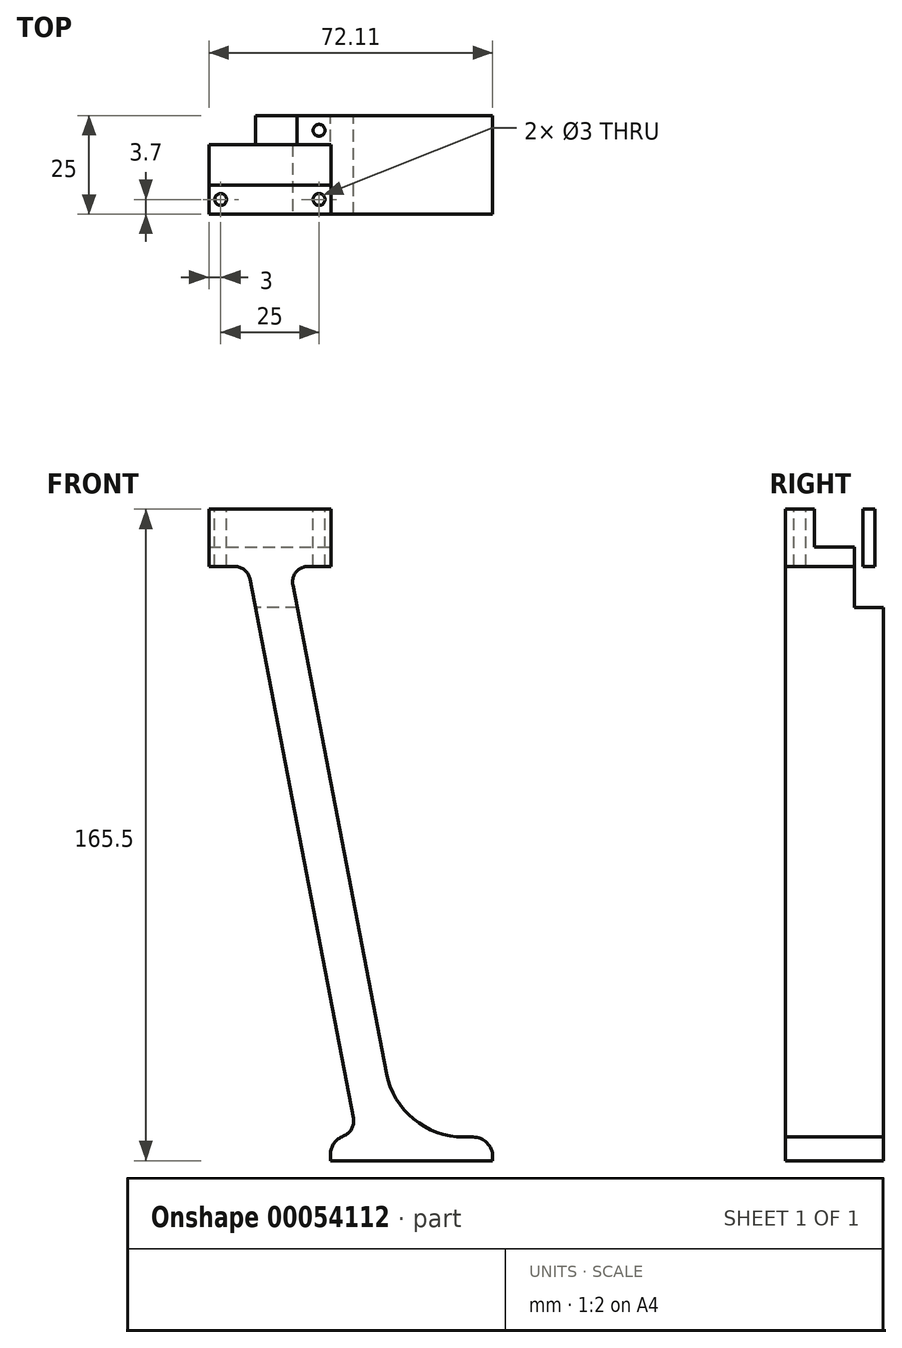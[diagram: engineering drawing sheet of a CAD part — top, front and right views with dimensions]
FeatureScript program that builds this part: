
annotation { "Feature Type Name" : "Feature", "Feature Type Description" : "" }
export const myFeature = defineFeature(function(context is Context, id is Id, definition is map)
    precondition{}
    {
        {
            var Q0;
            Q0=qCreatedBy(makeId("Front.planeOp"),FACE);
            var sketch = newSketch(context, id + "F0", { "sketchPlane" : qUnion([Q0])});
            skLineSegment(sketch, "E0.rect.bottom", {"start": v(12.5, -10) * mm, "end": v(1.92, -10) * mm});
            skLineSegment(sketch, "E0.rect.left", {"start": v(12.5, -10) * mm, "end": v(12.5, 4.5) * mm});
            skLineSegment(sketch, "E0.rect.right", {"start": v(-12.5, -10) * mm, "end": v(-12.5, 4.5) * mm});
            skPoint(sketch, "E0.rect.middle", {"position": v(0, 0) * mm});
            skLineSegment(sketch, "E1", {"start": v(-8.66, -10) * mm, "end": v(19.14, -155) * mm});
            skPoint(sketch, "E1.startSnap0", {"position": v(-12.5, 0) * mm});
            skLineSegment(sketch, "E2", {"start": v(1.92, -10) * mm, "end": v(29.71, -155) * mm});
            skPoint(sketch, "E3.orphan", {"position": v(-10.58, 0) * mm});
            skLineSegment(sketch, "E4.trimOffspring", {"start": v(-8.66, -10) * mm, "end": v(-12.5, -10) * mm});
            skLineSegment(sketch, "E5.bottom", {"start": v(12.4, -155) * mm, "end": v(19.14, -155) * mm});
            skLineSegment(sketch, "E5.top", {"start": v(12.4, -161) * mm, "end": v(53.6, -161) * mm});
            skLineSegment(sketch, "E5.left", {"start": v(12.4, -155) * mm, "end": v(12.4, -161) * mm});
            skLineSegment(sketch, "E5.right", {"start": v(53.6, -155) * mm, "end": v(53.6, -161) * mm});
            skLineSegment(sketch, "E6.trimOffspring", {"start": v(29.71, -155) * mm, "end": v(53.6, -155) * mm});
            skLineSegment(sketch, "E7", {"start": v(12.5, 4.5) * mm, "end": v(-12.5, 4.5) * mm});
            skPoint(sketch, "E8.orphan", {"position": v(12.5, 10) * mm});
            skPoint(sketch, "E9.orphan", {"position": v(-12.5, 10) * mm});
            skSolve(sketch);
        }
        {
            var Q0;
            Q0=makeQuery(id+"F0.imprint","IMPRINT",FACE,{"disambiguationData":[TD([[makeQuery(id+"F0.imprint","IMPRINT",EDGE,{"derivedFrom":sQuery(id+"F0.wireOp",EDGE,"E0.rect.bottom")}),-1.0]])]});
            var Q1;
            Q1 = qSketchRegion(id + "F2", true);
            extrude(context, id + "F1", {"entities" : qUnion([Q0, Q1]), "depth" : 25 * mm});
        }
        {
            var Q0;
            Q0=makeQuery(id+"F1.opExtrude","SWEPT_FACE",FACE,{"disambiguationData":[OSD([sQuery(id+"F0.wireOp",EDGE,"E0.rect.left")])]});
            var sketch = newSketch(context, id + "F2", { "sketchPlane" : qUnion([Q0])});
            skPoint(sketch, "E10.centerSnap0", {"position": v(-12.5, -10) * mm});
            skLineSegment(sketch, "E11.rect.bottom", {"start": v(-7.4, -5.1) * mm, "end": v(-17.6, -5.1) * mm});
            skLineSegment(sketch, "E11.rect.top", {"start": v(-7.4, 5.1) * mm, "end": v(-17.6, 5.1) * mm});
            skLineSegment(sketch, "E11.rect.left", {"start": v(-7.4, -5.1) * mm, "end": v(-7.4, 5.1) * mm});
            skLineSegment(sketch, "E11.rect.right", {"start": v(-17.6, -5.1) * mm, "end": v(-17.6, 5.1) * mm});
            skPoint(sketch, "E11.rect.middle", {"position": v(-12.5, 0) * mm});
            skSolve(sketch);
        }
        {
            var Q0;
            Q0=makeQuery(id+"F2.imprint","IMPRINT",FACE,{"disambiguationData":[TD([[makeQuery(id+"F2.imprint","IMPRINT",EDGE,{"derivedFrom":sQuery(id+"F2.wireOp",EDGE,"E11.rect.bottom")}),-1.0]])]});
            extrude(context, id + "F3", {"entities" : qUnion([Q0]), "operationType" : NewBodyOperationType.REMOVE, "oppositeDirection" : true, "depth" : 25 * mm});
        }
        {
            var Q0;
            Q0 = qSketchRegion(id + "F2", true);
            extrude(context, id + "F4", {"entities" : qUnion([Q0]), "operationType" : NewBodyOperationType.REMOVE, "oppositeDirection" : true, "depth" : 16 * mm});
        }
        {
            var Q0;
            Q0=makeQuery(id+"F1.opExtrude","SWEPT_FACE",FACE,{"disambiguationData":[OSD([sQuery(id+"F0.wireOp",EDGE,"E0.rect.right")])]});
            extrude(context, id + "F5", {"entities" : qUnion([Q0]), "operationType" : NewBodyOperationType.ADD, "depth" : 6 * mm});
        }
        {
            var Q0;
            {var subQ0=sQuery(id+"F0.wireOp",EDGE,"E7");var subQ1=sQuery(id+"F0.wireOp",EDGE,"E0.rect.right");var subQ5=makeQuery(id+"F3.opExtrude","SWEPT_FACE",FACE,{"disambiguationData":[OSD([sQuery(id+"F2.wireOp",EDGE,"E11.rect.left")])]});var subQ6=makeQuery(id+"F1.opExtrude","SWEPT_FACE",FACE,{"disambiguationData":[OSD([subQ0])]});Q0=makeQuery(id+"F5.boolean.opBoolean","MERGE",FACE,{"derivedFrom":[makeQuery(id+"F3.boolean.opBoolean","SPLIT",FACE,{"disambiguationData":[TD([subQ5])],"derivedFrom":subQ6}),makeQuery(id+"F5.opExtrude","SWEPT_FACE",FACE,{"disambiguationData":[OSD([subQ1,subQ0]),TDD([makeQuery(id+"F3.boolean.opBoolean","SPLIT",EDGE,{"disambiguationData":[TD([subQ5])],"derivedFrom":makeQuery(id+"F1.opExtrude","SWEPT_EDGE",EDGE,{"disambiguationData":[OSD([subQ1,subQ0])]})})])]})]});}
            var sketch = newSketch(context, id + "F6", { "sketchPlane" : qUnion([Q0])});
            skCircle(sketch, "E12", {"center": v(-15.5, -3.7) * mm, "radius": 1.5 * mm});
            skPoint(sketch, "E12.centerSnap0", {"position": v(-18.5, -3.7) * mm});
            skLineSegment(sketch, "E13", {"start": v(-3, 0) * mm, "end": v(-3, -7.4) * mm, "construction": true});
            skCircle(sketch, "E14.MirrorC", {"center": v(9.5, -3.7) * mm, "radius": 1.5 * mm});
            skSolve(sketch);
        }
        {
            var Q0;
            Q0=makeQuery(id+"F6.imprint","IMPRINT",FACE,{"disambiguationData":[TD([[makeQuery(id+"F6.imprint","IMPRINT",EDGE,{"derivedFrom":sQuery(id+"F6.wireOp",EDGE,"E12")}),1.0]])]});
            var Q1;
            Q1=makeQuery(id+"F6.imprint","IMPRINT",FACE,{"disambiguationData":[TD([[makeQuery(id+"F6.imprint","IMPRINT",EDGE,{"derivedFrom":sQuery(id+"F6.wireOp",EDGE,"E14.MirrorC")}),-1.0]])]});
            extrude(context, id + "F7", {"entities" : qUnion([Q0, Q1]), "operationType" : NewBodyOperationType.REMOVE, "oppositeDirection" : true, "depth" : 25 * mm});
        }
        {
            var Q0;
            {var subQ0=sQuery(id+"F0.wireOp",EDGE,"E7");var subQ1=sQuery(id+"F0.wireOp",EDGE,"E0.rect.right");var subQ5=makeQuery(id+"F3.opExtrude","SWEPT_FACE",FACE,{"disambiguationData":[OSD([sQuery(id+"F2.wireOp",EDGE,"E11.rect.right")])]});var subQ6=makeQuery(id+"F1.opExtrude","SWEPT_FACE",FACE,{"disambiguationData":[OSD([subQ0])]});Q0=makeQuery(id+"F5.boolean.opBoolean","MERGE",FACE,{"derivedFrom":[makeQuery(id+"F3.boolean.opBoolean","SPLIT",FACE,{"disambiguationData":[TD([subQ5])],"derivedFrom":subQ6}),makeQuery(id+"F5.opExtrude","SWEPT_FACE",FACE,{"disambiguationData":[OSD([subQ1,subQ0]),TDD([makeQuery(id+"F3.boolean.opBoolean","SPLIT",EDGE,{"disambiguationData":[TD([subQ5])],"derivedFrom":makeQuery(id+"F1.opExtrude","SWEPT_EDGE",EDGE,{"disambiguationData":[OSD([subQ1,subQ0])]})})])]})]});}
            var sketch = newSketch(context, id + "F8", { "sketchPlane" : qUnion([Q0])});
            skCircle(sketch, "E15", {"center": v(-15.5, -21.3) * mm, "radius": 1.5 * mm});
            skPoint(sketch, "E15.centerSnap0", {"position": v(-18.5, -21.3) * mm});
            skLineSegment(sketch, "E16", {"start": v(-3, -17.6) * mm, "end": v(-3, -25) * mm, "construction": true});
            skCircle(sketch, "E17.MirrorC", {"center": v(9.5, -21.3) * mm, "radius": 1.5 * mm});
            skSolve(sketch);
        }
        {
            var Q0;
            Q0 = qSketchRegion(id + "F8", true);
            extrude(context, id + "F9", {"entities" : qUnion([Q0]), "operationType" : NewBodyOperationType.REMOVE, "oppositeDirection" : true, "depth" : 25 * mm});
        }
        {
            var Q0;
            Q0=makeQuery(id+"F1.opExtrude","SWEPT_EDGE",EDGE,{"disambiguationData":[OSD([sQuery(id+"F0.wireOp",EDGE,"E0.rect.bottom"),sQuery(id+"F0.wireOp",EDGE,"E2")])]});
            var Q1;
            Q1=makeQuery(id+"F1.opExtrude","SWEPT_EDGE",EDGE,{"disambiguationData":[OSD([sQuery(id+"F0.wireOp",EDGE,"E1"),sQuery(id+"F0.wireOp",EDGE,"E4.trimOffspring")])]});
            fillet(context, id + "F10", {"entities" : qUnion([Q0, Q1]), "radius" : 4 * mm, "tangentPropagation" : true, "allowEdgeOverflow" : false});
        }
        {
            var Q0;
            Q0=makeQuery(id+"F1.opExtrude","SWEPT_EDGE",EDGE,{"disambiguationData":[OSD([sQuery(id+"F0.wireOp",EDGE,"E2"),sQuery(id+"F0.wireOp",EDGE,"E6.trimOffspring")])]});
            fillet(context, id + "F11", {"entities" : qUnion([Q0]), "radius" : 20 * mm, "tangentPropagation" : true, "allowEdgeOverflow" : false});
        }
        {
            var Q0;
            Q0=makeQuery(id+"F1.opExtrude","SWEPT_EDGE",EDGE,{"disambiguationData":[OSD([sQuery(id+"F0.wireOp",EDGE,"E1"),sQuery(id+"F0.wireOp",EDGE,"E5.bottom")])]});
            fillet(context, id + "F12", {"entities" : qUnion([Q0]), "radius" : 4 * mm, "tangentPropagation" : true, "allowEdgeOverflow" : false});
        }
        {
            var Q0;
            Q0=makeQuery(id+"F1.opExtrude","SWEPT_EDGE",EDGE,{"disambiguationData":[OSD([sQuery(id+"F0.wireOp",EDGE,"E5.bottom"),sQuery(id+"F0.wireOp",EDGE,"E5.left")])]});
            var Q1;
            Q1=makeQuery(id+"F1.opExtrude","SWEPT_EDGE",EDGE,{"disambiguationData":[OSD([sQuery(id+"F0.wireOp",EDGE,"E5.right"),sQuery(id+"F0.wireOp",EDGE,"E6.trimOffspring")])]});
            fillet(context, id + "F13", {"entities" : qUnion([Q0, Q1]), "radius" : 5 * mm, "tangentPropagation" : true, "allowEdgeOverflow" : false});
        }
    });
